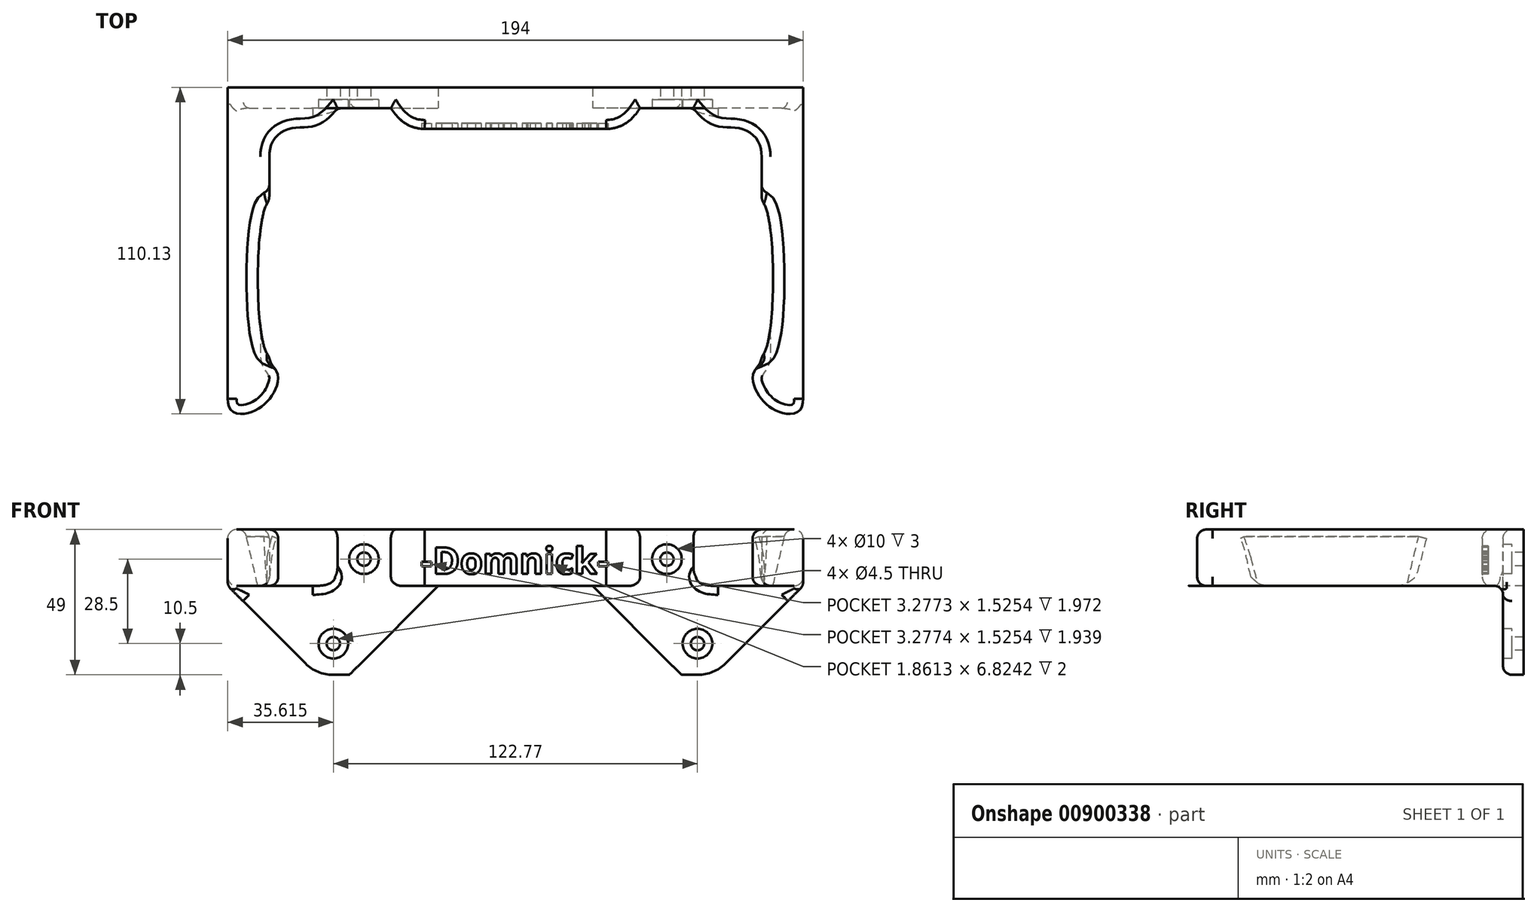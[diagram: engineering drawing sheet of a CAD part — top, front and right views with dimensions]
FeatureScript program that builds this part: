
annotation { "Feature Type Name" : "Feature", "Feature Type Description" : "" }
export const myFeature = defineFeature(function(context is Context, id is Id, definition is map)
    precondition{}
    {
        {
            var Q0;
            Q0=qCreatedBy(makeId("Top.planeOp"),FACE);
            var sketch = newSketch(context, id + "F0", { "sketchPlane" : qUnion([Q0])});
            skLineSegment(sketch, "E0", {"start": v(-97, -55) * mm, "end": v(-97, 50) * mm});
            skLineSegment(sketch, "E1", {"start": v(-83, 35.04) * mm, "end": v(-83, -31.62) * mm});
            skLineSegment(sketch, "E2", {"start": v(-60, -48) * mm, "end": v(-42, -48) * mm});
            skLineSegment(sketch, "E3", {"start": v(-42, -48) * mm, "end": v(-42, -48) * mm});
            skLineSegment(sketch, "E4", {"start": v(-30.59, -41) * mm, "end": v(0, -41) * mm});
            skLineSegment(sketch, "E5", {"start": v(0, -41) * mm, "end": v(0, -55) * mm});
            skLineSegment(sketch, "E6", {"start": v(0, -55) * mm, "end": v(-97, -55) * mm});
            skPoint(sketch, "E7.visualSharp", {"position": v(-42, -41) * mm});
            skFitSpline(sketch, "E8", {"points": [v(-60, -48) * mm, v(-74.68, -41.36) * mm, v(-83, -31.62) * mm], "startDerivative": vector(-34.71, 44.32) * mm, "endDerivative": vector(0, 42.54) * mm});
            skFitSpline(sketch, "E9", {"points": [v(-30.59, -41) * mm, v(-42, -48) * mm], "startDerivative": vector(-9.38, -0.32) * mm, "endDerivative": vector(-11.65, -18.3) * mm});
            skFitSpline(sketch, "E10", {"points": [v(-83, 35.04) * mm, v(-80.16, 41.61) * mm, v(-83.93, 51.2) * mm, v(-93.13, 55.1) * mm, v(-97, 50) * mm], "startDerivative": vector(-0.85, 48.06) * mm, "endDerivative": vector(-0.21, -51.67) * mm});
            skLineSegment(sketch, "E11", {"start": v(-42, -48) * mm, "end": v(-42, -55) * mm});
            skLineSegment(sketch, "E12", {"start": v(-42, -48) * mm, "end": v(0, -48) * mm});
            skLineSegment(sketch, "E13", {"start": v(-60, -48) * mm, "end": v(-60, -55) * mm});
            skLineSegment(sketch, "E14", {"start": v(-60, -48) * mm, "end": v(-97, -48) * mm});
            skSolve(sketch);
        }
        {
            var Q0;
            {var subQ1=sQuery(id+"F0.wireOp",EDGE,"E0");Q0=makeQuery(id+"F0.imprint","IMPRINT",FACE,{"disambiguationData":[TD([[makeQuery(id+"F0.imprint","IMPRINT",EDGE,{"derivedFrom":subQ1}),-1.0]])]});}
            var Q1;
            {var subQ0=sQuery(id+"F0.wireOp",EDGE,"E13");Q1=makeQuery(id+"F0.imprint","IMPRINT",FACE,{"disambiguationData":[TD([[makeQuery(id+"F0.imprint","IMPRINT",EDGE,{"derivedFrom":subQ0}),-1.0]])]});}
            var Q2;
            Q2=makeQuery(id+"F0.imprint","IMPRINT",FACE,{"disambiguationData":[TD([[makeQuery(id+"F0.imprint","IMPRINT",EDGE,{"derivedFrom":sQuery(id+"F0.wireOp",EDGE,"E1")}),-1.0]])]});
            extrude(context, id + "F1", {"entities" : qUnion([Q0, Q1, Q2]), "oppositeDirection" : true, "depth" : 22 * mm, "hasSecondDirection" : true, "secondDirectionOppositeDirection" : true, "secondDirectionDepth" : 3 * mm});
        }
        {
            var Q0;
            Q0=makeQuery(id+"F0.imprint","IMPRINT",FACE,{"disambiguationData":[TD([[makeQuery(id+"F0.imprint","IMPRINT",EDGE,{"derivedFrom":sQuery(id+"F0.wireOp",EDGE,"E2")}),-1.0]])]});
            var Q1;
            {var subQ4=sQuery(id+"F0.wireOp",EDGE,"E11");Q1=makeQuery(id+"F0.imprint","IMPRINT",FACE,{"disambiguationData":[TD([[makeQuery(id+"F0.imprint","IMPRINT",EDGE,{"derivedFrom":subQ4}),1.0]])]});}
            var Q2;
            {var subQ4=sQuery(id+"F0.wireOp",EDGE,"E13");Q2=makeQuery(id+"F0.imprint","IMPRINT",FACE,{"disambiguationData":[TD([[makeQuery(id+"F0.imprint","IMPRINT",EDGE,{"derivedFrom":subQ4}),-1.0]])]});}
            extrude(context, id + "F2", {"entities" : qUnion([Q0, Q1, Q2]), "operationType" : NewBodyOperationType.ADD, "oppositeDirection" : true, "depth" : 22 * mm, "hasSecondDirection" : true, "secondDirectionOppositeDirection" : false, "secondDirectionDepth" : 27 * mm});
        }
        {
            var Q0;
            Q0=makeQuery(id+"F2.opExtrude","CAP_EDGE",EDGE,{"disambiguationData":[OSD([sQuery(id+"F0.wireOp",EDGE,"E0")])],"isStart":true});
            chamfer(context, id + "F3", {"entities" : qUnion([Q0]), "width" : 30 * mm, "tangentPropagation" : true});
        }
        {
            var Q0;
            {var subQ0=sQuery(id+"F0.wireOp",EDGE,"E4");Q0=makeQuery(id+"F0.imprint","IMPRINT",FACE,{"disambiguationData":[TD([[makeQuery(id+"F0.imprint","IMPRINT",EDGE,{"derivedFrom":subQ0}),-1.0]])]});}
            extrude(context, id + "F4", {"entities" : qUnion([Q0]), "operationType" : NewBodyOperationType.ADD, "oppositeDirection" : true, "depth" : 22 * mm, "hasSecondDirection" : true, "secondDirectionOppositeDirection" : true, "secondDirectionDepth" : 3 * mm});
        }
        {
            var Q0;
            Q0=makeQuery(id+"F1.opExtrude","CAP_FACE",FACE,{"disambiguationData":[OSD([sQuery(id+"F0.wireOp",EDGE,"E0"),sQuery(id+"F0.wireOp",EDGE,"E1"),sQuery(id+"F0.wireOp",EDGE,"E6"),sQuery(id+"F0.wireOp",EDGE,"E8"),sQuery(id+"F0.wireOp",EDGE,"E10"),sQuery(id+"F0.wireOp",EDGE,"E13")])],"isStart":true});
            var sketch = newSketch(context, id + "F5", { "sketchPlane" : qUnion([Q0])});
            skLineSegment(sketch, "E15", {"start": v(-83, 35.04) * mm, "end": v(-83, -16.09) * mm});
            skFitSpline(sketch, "E16", {"points": [v(-83, 35.04) * mm, v(-83, -16.09) * mm], "startDerivative": vector(-15.48, -5.6) * mm, "endDerivative": vector(15.48, -6.32) * mm});
            skSolve(sketch);
        }
        {
            var Q0;
            Q0=makeQuery(id+"F5.imprint","IMPRINT",FACE,{"disambiguationData":[TD([[makeQuery(id+"F5.imprint","IMPRINT",EDGE,{"derivedFrom":sQuery(id+"F5.wireOp",EDGE,"E15")}),-1.0]])]});
            extrude(context, id + "F6", {"entities" : qUnion([Q0]), "operationType" : NewBodyOperationType.REMOVE, "oppositeDirection" : true, "depth" : 25 * mm, "hasDraft" : true, "draftAngle" : 13 * degree});
        }
        {
            var Q0;
            Q0=makeQuery(id+"F2.opExtrude","SWEPT_FACE",FACE,{"disambiguationData":[OSD([sQuery(id+"F0.wireOp",EDGE,"E2"),sQuery(id+"F0.wireOp",EDGE,"E12"),sQuery(id+"F0.wireOp",EDGE,"E14")])]});
            var sketch = newSketch(context, id + "F7", { "sketchPlane" : qUnion([Q0])});
            skLineSegment(sketch, "E17", {"start": v(56, 27) * mm, "end": v(26, -3) * mm});
            skSolve(sketch);
        }
        {
            var Q0;
            {var subQ0=sQuery(id+"F7.wireOp",EDGE,"E17");Q0=makeQuery(id+"F7.imprint","IMPRINT",FACE,{"disambiguationData":[TD([[makeQuery(id+"F7.imprint","IMPRINT",EDGE,{"derivedFrom":subQ0}),-1.0]])]});}
            extrude(context, id + "F8", {"entities" : qUnion([Q0]), "operationType" : NewBodyOperationType.REMOVE, "oppositeDirection" : true, "depth" : 25 * mm});
        }
        {
            var Q0;
            {var subQ0=sQuery(id+"F0.wireOp",EDGE,"E0");Q0=makeQuery(id+"F3.opChamfer","BLEND_EDGE",EDGE,{"blendedFrom":[makeQuery(id+"F2.opExtrude","CAP_EDGE",EDGE,{"disambiguationData":[OSD([subQ0])],"isStart":true}),makeQuery(id+"F2.opExtrude","CAP_FACE",FACE,{"disambiguationData":[OSD([subQ0,sQuery(id+"F0.wireOp",EDGE,"E2"),sQuery(id+"F0.wireOp",EDGE,"E5"),sQuery(id+"F0.wireOp",EDGE,"E6"),sQuery(id+"F0.wireOp",EDGE,"E12"),sQuery(id+"F0.wireOp",EDGE,"E14")])],"isStart":true})],"blendedInto":[makeQuery(id+"F2.opExtrude","CAP_FACE",FACE,{"disambiguationData":[OSD([subQ0,sQuery(id+"F0.wireOp",EDGE,"E2"),sQuery(id+"F0.wireOp",EDGE,"E5"),sQuery(id+"F0.wireOp",EDGE,"E6"),sQuery(id+"F0.wireOp",EDGE,"E12"),sQuery(id+"F0.wireOp",EDGE,"E14")])],"isStart":true})]});}
            var Q1;
            Q1=makeQuery(id+"F8.boolean.opBoolean","COPY",EDGE,{"derivedFrom":makeQuery(id+"F8.opExtrude","SWEPT_EDGE",EDGE,{"disambiguationData":[OSD([sQuery(id+"F0.wireOp",EDGE,"E2"),sQuery(id+"F0.wireOp",EDGE,"E12"),sQuery(id+"F0.wireOp",EDGE,"E14"),sQuery(id+"F7.wireOp",EDGE,"E17")])]})});
            fillet(context, id + "F9", {"entities" : qUnion([Q0, Q1]), "radius" : 13 * mm, "tangentPropagation" : true, "allowEdgeOverflow" : false});
        }
        {
            var Q0;
            Q0=makeQuery(id+"F1.opExtrude","CAP_EDGE",EDGE,{"disambiguationData":[OSD([sQuery(id+"F0.wireOp",EDGE,"E8")])],"isStart":false});
            var Q1;
            Q1=makeQuery(id+"F1.opExtrude","CAP_EDGE",EDGE,{"disambiguationData":[OSD([sQuery(id+"F0.wireOp",EDGE,"E8")])],"isStart":true});
            var Q2;
            Q2=makeQuery(id+"F1.opExtrude","CAP_EDGE",EDGE,{"disambiguationData":[OSD([sQuery(id+"F0.wireOp",EDGE,"E1")])],"isStart":false});
            var Q3;
            Q3=makeQuery(id+"F1.opExtrude","CAP_EDGE",EDGE,{"disambiguationData":[OSD([sQuery(id+"F0.wireOp",EDGE,"E1")])],"isStart":true});
            var Q4;
            Q4=makeQuery(id+"F1.opExtrude","CAP_EDGE",EDGE,{"disambiguationData":[OSD([sQuery(id+"F0.wireOp",EDGE,"E10")])],"isStart":true});
            var Q5;
            Q5=makeQuery(id+"F1.opExtrude","CAP_EDGE",EDGE,{"disambiguationData":[OSD([sQuery(id+"F0.wireOp",EDGE,"E10")])],"isStart":false});
            var Q6;
            Q6=makeQuery(id+"F1.opExtrude","CAP_EDGE",EDGE,{"disambiguationData":[OSD([sQuery(id+"F0.wireOp",EDGE,"E0")])],"isStart":false});
            var Q7;
            Q7=makeQuery(id+"F1.opExtrude","CAP_EDGE",EDGE,{"disambiguationData":[OSD([sQuery(id+"F0.wireOp",EDGE,"E0")])],"isStart":true});
            var Q8;
            Q8=makeQuery(id+"F2.opExtrude","CAP_EDGE",EDGE,{"disambiguationData":[OSD([sQuery(id+"F0.wireOp",EDGE,"E2"),sQuery(id+"F0.wireOp",EDGE,"E12")])],"isStart":false});
            var Q9;
            Q9=makeQuery(id+"F4.opExtrude","CAP_EDGE",EDGE,{"disambiguationData":[OSD([sQuery(id+"F0.wireOp",EDGE,"E9")])],"isStart":false});
            var Q10;
            Q10=makeQuery(id+"F4.opExtrude","CAP_EDGE",EDGE,{"disambiguationData":[OSD([sQuery(id+"F0.wireOp",EDGE,"E4")])],"isStart":false});
            var Q11;
            Q11=makeQuery(id+"F4.opExtrude","CAP_EDGE",EDGE,{"disambiguationData":[OSD([sQuery(id+"F0.wireOp",EDGE,"E9")])],"isStart":true});
            var Q12;
            Q12=makeQuery(id+"F4.opExtrude","CAP_EDGE",EDGE,{"disambiguationData":[OSD([sQuery(id+"F0.wireOp",EDGE,"E4")])],"isStart":true});
            var Q13;
            {var subQ0=sQuery(id+"F0.wireOp",EDGE,"E12");var subQ1=sQuery(id+"F0.wireOp",EDGE,"E5");var subQ2=sQuery(id+"F0.wireOp",EDGE,"E13");var subQ3=sQuery(id+"F0.wireOp",EDGE,"E6");Q13=makeQuery(id+"F6.boolean.opBoolean","INTERSECT",EDGE,{"derivedFrom":[makeQuery(id+"F4.boolean.opBoolean","MERGE",FACE,{"derivedFrom":[makeQuery(id+"F2.boolean.opBoolean","MERGE",FACE,{"derivedFrom":[makeQuery(id+"F1.opExtrude","CAP_FACE",FACE,{"disambiguationData":[OSD([sQuery(id+"F0.wireOp",EDGE,"E0"),sQuery(id+"F0.wireOp",EDGE,"E1"),subQ3,sQuery(id+"F0.wireOp",EDGE,"E8"),sQuery(id+"F0.wireOp",EDGE,"E10"),subQ2])],"isStart":false}),makeQuery(id+"F2.opExtrude","CAP_FACE",FACE,{"disambiguationData":[OSD([sQuery(id+"F0.wireOp",EDGE,"E2"),subQ1,subQ3,subQ0,subQ2])],"isStart":false})]}),makeQuery(id+"F4.opExtrude","CAP_FACE",FACE,{"disambiguationData":[OSD([sQuery(id+"F0.wireOp",EDGE,"E4"),subQ1,sQuery(id+"F0.wireOp",EDGE,"E9"),subQ0])],"isStart":false})]}),makeQuery(id+"F6.opExtrude","SWEPT_FACE",FACE,{"disambiguationData":[OSD([sQuery(id+"F5.wireOp",EDGE,"E16")])]})]});}
            var Q14;
            Q14=makeQuery(id+"F6.boolean.opBoolean","COPY",EDGE,{"derivedFrom":makeQuery(id+"F6.opExtrude","CAP_EDGE",EDGE,{"disambiguationData":[OSD([sQuery(id+"F5.wireOp",EDGE,"E16")])],"isStart":true})});
            var Q15;
            Q15=makeQuery(id+"F6.boolean.opBoolean","INTERSECT",EDGE,{"derivedFrom":[makeQuery(id+"F1.opExtrude","SWEPT_FACE",FACE,{"disambiguationData":[OSD([sQuery(id+"F0.wireOp",EDGE,"E1")])]}),makeQuery(id+"F6.opExtrude","SWEPT_FACE",FACE,{"disambiguationData":[OSD([sQuery(id+"F5.wireOp",EDGE,"E16")])]})]});
            var Q16;
            Q16=makeQuery(id+"F6.boolean.opBoolean","INTERSECT",EDGE,{"derivedFrom":[makeQuery(id+"F1.opExtrude","SWEPT_FACE",FACE,{"disambiguationData":[OSD([sQuery(id+"F0.wireOp",EDGE,"E10")])]}),makeQuery(id+"F6.opExtrude","SWEPT_FACE",FACE,{"disambiguationData":[OSD([sQuery(id+"F5.wireOp",EDGE,"E16")])]})]});
            var Q17;
            Q17=makeQuery(id+"F2.boolean.opBoolean","INTERSECT",EDGE,{"derivedFrom":[makeQuery(id+"F1.opExtrude","CAP_FACE",FACE,{"disambiguationData":[OSD([sQuery(id+"F0.wireOp",EDGE,"E0"),sQuery(id+"F0.wireOp",EDGE,"E1"),sQuery(id+"F0.wireOp",EDGE,"E6"),sQuery(id+"F0.wireOp",EDGE,"E8"),sQuery(id+"F0.wireOp",EDGE,"E10"),sQuery(id+"F0.wireOp",EDGE,"E13")])],"isStart":true}),makeQuery(id+"F2.opExtrude","SWEPT_FACE",FACE,{"disambiguationData":[OSD([sQuery(id+"F0.wireOp",EDGE,"E2"),sQuery(id+"F0.wireOp",EDGE,"E12"),sQuery(id+"F0.wireOp",EDGE,"E14")])]})]});
            var Q18;
            Q18=makeQuery(id+"F4.opExtrude","CAP_EDGE",EDGE,{"disambiguationData":[OSD([sQuery(id+"F0.wireOp",EDGE,"E12")])],"isStart":true});
            var Q19;
            Q19=makeQuery(id+"F3.opChamfer","BLEND_EDGE",EDGE,{"blendedFrom":[makeQuery(id+"F2.opExtrude","CAP_EDGE",EDGE,{"disambiguationData":[OSD([sQuery(id+"F0.wireOp",EDGE,"E0")])],"isStart":true}),makeQuery(id+"F2.opExtrude","SWEPT_FACE",FACE,{"disambiguationData":[OSD([sQuery(id+"F0.wireOp",EDGE,"E2"),sQuery(id+"F0.wireOp",EDGE,"E12"),sQuery(id+"F0.wireOp",EDGE,"E14")])]})],"blendedInto":[makeQuery(id+"F2.opExtrude","SWEPT_FACE",FACE,{"disambiguationData":[OSD([sQuery(id+"F0.wireOp",EDGE,"E2"),sQuery(id+"F0.wireOp",EDGE,"E12"),sQuery(id+"F0.wireOp",EDGE,"E14")])]})]});
            var Q20;
            {var subQ0=sQuery(id+"F0.wireOp",EDGE,"E14");var subQ1=sQuery(id+"F0.wireOp",EDGE,"E12");var subQ2=sQuery(id+"F0.wireOp",EDGE,"E2");var subQ3=sQuery(id+"F0.wireOp",EDGE,"E0");Q20=makeQuery(id+"F9.opFillet","BLEND_EDGE",EDGE,{"blendedFrom":[makeQuery(id+"F3.opChamfer","BLEND_EDGE",EDGE,{"blendedFrom":[makeQuery(id+"F2.opExtrude","CAP_EDGE",EDGE,{"disambiguationData":[OSD([subQ3])],"isStart":true}),makeQuery(id+"F2.opExtrude","CAP_FACE",FACE,{"disambiguationData":[OSD([subQ3,subQ2,sQuery(id+"F0.wireOp",EDGE,"E5"),sQuery(id+"F0.wireOp",EDGE,"E6"),subQ1,subQ0])],"isStart":true})],"blendedInto":[makeQuery(id+"F2.opExtrude","CAP_FACE",FACE,{"disambiguationData":[OSD([subQ3,subQ2,sQuery(id+"F0.wireOp",EDGE,"E5"),sQuery(id+"F0.wireOp",EDGE,"E6"),subQ1,subQ0])],"isStart":true})]}),makeQuery(id+"F2.opExtrude","SWEPT_FACE",FACE,{"disambiguationData":[OSD([subQ2,subQ1,subQ0])]})],"blendedInto":[makeQuery(id+"F2.opExtrude","SWEPT_FACE",FACE,{"disambiguationData":[OSD([subQ2,subQ1,subQ0])]})]});}
            var Q21;
            Q21=makeQuery(id+"F2.opExtrude","CAP_EDGE",EDGE,{"disambiguationData":[OSD([sQuery(id+"F0.wireOp",EDGE,"E2"),sQuery(id+"F0.wireOp",EDGE,"E12"),sQuery(id+"F0.wireOp",EDGE,"E14")])],"isStart":true});
            var Q22;
            {var subQ0=sQuery(id+"F0.wireOp",EDGE,"E0");Q22=makeQuery(id+"F3.opChamfer","BLEND_EDGE",EDGE,{"blendedFrom":[makeQuery(id+"F2.opExtrude","CAP_EDGE",EDGE,{"disambiguationData":[OSD([subQ0])],"isStart":true}),makeQuery(id+"F2.boolean.opBoolean","MERGE",FACE,{"derivedFrom":[makeQuery(id+"F1.opExtrude","SWEPT_FACE",FACE,{"disambiguationData":[OSD([subQ0])]}),makeQuery(id+"F2.opExtrude","SWEPT_FACE",FACE,{"disambiguationData":[OSD([subQ0])]})]})],"blendedInto":[makeQuery(id+"F2.boolean.opBoolean","MERGE",FACE,{"derivedFrom":[makeQuery(id+"F1.opExtrude","SWEPT_FACE",FACE,{"disambiguationData":[OSD([subQ0])]}),makeQuery(id+"F2.opExtrude","SWEPT_FACE",FACE,{"disambiguationData":[OSD([subQ0])]})]})]});}
            fillet(context, id + "F10", {"entities" : qUnion([Q0, Q1, Q2, Q3, Q4, Q5, Q6, Q7, Q8, Q9, Q10, Q11, Q12, Q13, Q14, Q15, Q16, Q17, Q18, Q19, Q20, Q21, Q22]), "radius" : 3 * mm, "tangentPropagation" : true, "allowEdgeOverflow" : false});
        }
        {
            var Q0;
            Q0=makeQuery(id+"F2.opExtrude","SWEPT_FACE",FACE,{"disambiguationData":[OSD([sQuery(id+"F0.wireOp",EDGE,"E2"),sQuery(id+"F0.wireOp",EDGE,"E12")])]});
            var sketch = newSketch(context, id + "F11", { "sketchPlane" : qUnion([Q0])});
            skCircle(sketch, "E18", {"center": v(51.08, -12) * mm, "radius": 5 * mm});
            skPoint(sketch, "E18.centerSnap0", {"position": v(51.08, -19) * mm});
            skPoint(sketch, "E18.centerSnap1", {"position": v(46.08, -12) * mm});
            skCircle(sketch, "E19", {"center": v(51.08, -12) * mm, "radius": 2.25 * mm});
            skCircle(sketch, "E20", {"center": v(61.38, 16.5) * mm, "radius": 5 * mm});
            skCircle(sketch, "E21", {"center": v(61.38, 16.5) * mm, "radius": 2.25 * mm});
            skSolve(sketch);
        }
        {
            var Q0;
            Q0=qSketchRegion(id+"F11",true);
            var Q1;
            Q1=sQuery(id+"F11.wireOp",EDGE,"E19");
            extrude(context, id + "F12", {"entities" : qUnion([Q0]), "operationType" : NewBodyOperationType.REMOVE, "surfaceEntities" : qUnion([Q1]), "oppositeDirection" : true, "depth" : 3 * mm});
        }
        {
            var Q0;
            Q0=makeQuery(id+"F11.imprint","IMPRINT",FACE,{"disambiguationData":[TD([[makeQuery(id+"F11.imprint","IMPRINT",EDGE,{"derivedFrom":sQuery(id+"F11.wireOp",EDGE,"E21")}),1.0]])]});
            var Q1;
            Q1=makeQuery(id+"F11.imprint","IMPRINT",FACE,{"disambiguationData":[TD([[makeQuery(id+"F11.imprint","IMPRINT",EDGE,{"derivedFrom":sQuery(id+"F11.wireOp",EDGE,"E19")}),1.0]])]});
            var Q2;
            Q2=sQuery(id+"F11.wireOp",EDGE,"E19");
            extrude(context, id + "F13", {"entities" : qUnion([Q0, Q1]), "operationType" : NewBodyOperationType.REMOVE, "surfaceEntities" : qUnion([Q2]), "oppositeDirection" : true, "depth" : 25 * mm});
        }
        {
            var Q0;
            Q0=makeQuery(id+"F1.opExtrude","SWEPT_BODY",BODY,{"disambiguationData":[OSD([sQuery(id+"F0.wireOp",EDGE,"E0"),sQuery(id+"F0.wireOp",EDGE,"E1"),sQuery(id+"F0.wireOp",EDGE,"E6"),sQuery(id+"F0.wireOp",EDGE,"E8"),sQuery(id+"F0.wireOp",EDGE,"E10"),sQuery(id+"F0.wireOp",EDGE,"E13")])]});
            var Q1;
            Q1=qCreatedBy(makeId("Right.planeOp"),FACE);
            mirror(context, id + "F14", {"operationType" : NewBodyOperationType.ADD, "entities" : qUnion([Q0]), "mirrorPlane" : qUnion([Q1])});
        }
        {
            var Q0;
            Q0=qCreatedBy(makeId("Front.planeOp"),FACE);
            var sketch = newSketch(context, id + "F15", { "sketchPlane" : qUnion([Q0])});
            skLineSegment(sketch, "E22", {"start": v(0, 27) * mm, "end": v(0, -22) * mm});
            skLineSegment(sketch, "E23", {"start": v(-30, 0) * mm, "end": v(30, 0) * mm});
            skSolve(sketch);
        }
        {
            var Q0;
            Q0=makeQuery(id+"F1.opExtrude","SWEPT_BODY",BODY,{"disambiguationData":[OSD([sQuery(id+"F0.wireOp",EDGE,"E0"),sQuery(id+"F0.wireOp",EDGE,"E1"),sQuery(id+"F0.wireOp",EDGE,"E6"),sQuery(id+"F0.wireOp",EDGE,"E8"),sQuery(id+"F0.wireOp",EDGE,"E10"),sQuery(id+"F0.wireOp",EDGE,"E13")])]});
            var Q1;
            Q1=sQuery(id+"F15.wireOp",EDGE,"E23");
            transform(context, id + "F16", {"entities" : qUnion([Q0]), "transformType" : TransformType.ROTATION, "transformAxis" : qUnion([Q1]), "angle" : 180 * degree, "makeCopy" : false});
        }
        {
            var Q0;
            {var subQ0=makeQuery(id+"F4.opExtrude","SWEPT_FACE",FACE,{"disambiguationData":[OSD([sQuery(id+"F0.wireOp",EDGE,"E4")])]});Q0=makeQuery(id+"F14.boolean.opBoolean","MERGE",FACE,{"derivedFrom":[subQ0,makeQuery(id+"F14.opPattern","COPY",FACE,{"derivedFrom":subQ0,"instanceName":"1"})]});}
            var sketch = newSketch(context, id + "F17", { "sketchPlane" : qUnion([Q0])});
            skText(sketch, "E24", { "text": "-Domnick-", "fontName": "OpenSans-Bold.ttf"});
            const initialGuessF17  = {"E24": [-0.03198, 0.007, 1, 0, 0.009]};
            skSetInitialGuess(sketch, initialGuessF17);
            skSolve(sketch);
        }
        {
            var Q0;
            Q0=qSketchRegion(id+"F17",true);
            extrude(context, id + "F18", {"entities" : qUnion([Q0]), "operationType" : NewBodyOperationType.REMOVE, "oppositeDirection" : true, "depth" : 2 * mm});
        }
    });
